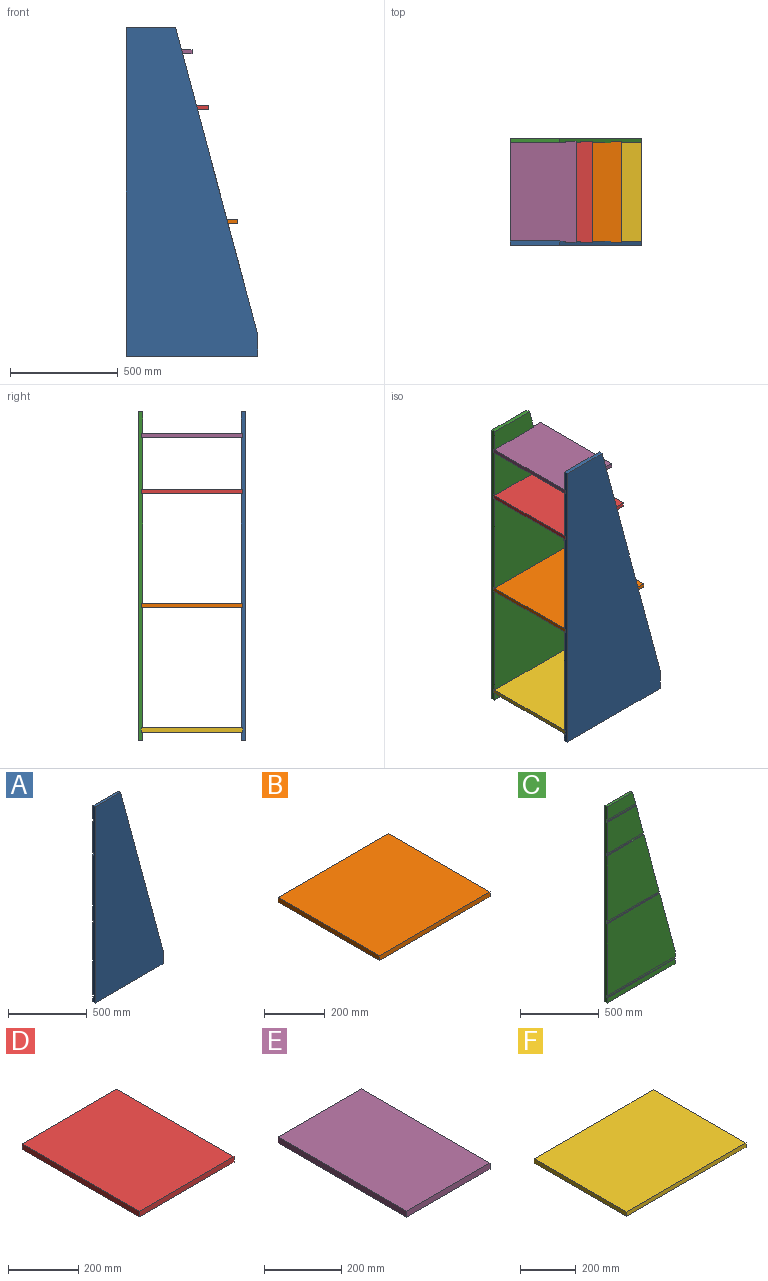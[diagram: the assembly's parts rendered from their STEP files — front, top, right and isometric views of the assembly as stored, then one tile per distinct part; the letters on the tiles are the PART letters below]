
ASSEMBLY  parts=6 mates=16
PART A: 23 faces, bbox 609.6x19.1x1524 mm
  f0: plane 255.81x101.6mm, normal (0,1,0), area 24608.2mm2, adj f5,f6,f7,f17
  f1: plane 508x466.73mm, normal (0,1,0), area 202534.2mm2, adj f5,f7,f11,f15
  f2: plane 609.6x558.8mm, normal (0,1,0), area 305212.9mm2, adj f4,f5,f7,f14,f20
  f3: plane 325.55x241.3mm, normal (0,1,0), area 70757.3mm2, adj f5,f7,f12,f18
  f4: plane 101.6x19.05mm, normal (1,0,0), area 1814.5mm2, adj f2,f5,f8,f9,f10,f20,f21,f22
  f5: plane 1422.4x381mm, normal (0.97,0,0.26), area 27676.2mm2, adj f0,f1,f2,f3,f4,f6,f9,f11
  f6: plane 228.6x19.05mm, normal (0,0,1), area 4354.8mm2, adj f0,f5,f7,f9
  f7: plane 1524x19.05mm, normal (-1,0,0), area 28548.3mm2, adj f0,f1,f2,f3,f6,f8,f9,f10
  f8: plane 609.6x19.05mm, normal (0,0,-1), area 11612.9mm2, adj f4,f7,f9,f10
  f9: plane 1524x609.6mm, normal (0,-1,0), area 658063.2mm2, adj f4,f5,f6,f7,f8
  f10: plane 609.6x38.1mm, normal (0,1,0), area 23225.8mm2, adj f4,f7,f8,f21
  f11: plane 330.65x6.35mm, normal (0,0,1), area 2099.7mm2, adj f1,f5,f7,f13
  f12: plane 325.55x6.35mm, normal (0,0,-1), area 2067.2mm2, adj f3,f5,f7,f13
  f13: plane 330.65x19.05mm, normal (0,1,0), area 6250.3mm2, adj f5,f7,f11,f12
  f14: plane 471.83x6.35mm, normal (0,0,1), area 2996.1mm2, adj f2,f5,f7,f16
  f15: plane 466.73x6.35mm, normal (0,0,-1), area 2963.7mm2, adj f1,f5,f7,f16
  f16: plane 471.83x19.05mm, normal (0,1,0), area 8939.7mm2, adj f5,f7,f14,f15
  f17: plane 255.81x6.35mm, normal (0,0,-1), area 1624.4mm2, adj f0,f5,f7,f19
  f18: plane 260.92x6.35mm, normal (0,0,1), area 1656.8mm2, adj f3,f5,f7,f19
  f19: plane 260.92x19.05mm, normal (0,1,0), area 4921.9mm2, adj f5,f7,f17,f18
  f20: plane 609.6x6.35mm, normal (0,0,-1), area 3871mm2, adj f2,f4,f7,f22
  f21: plane 609.6x6.35mm, normal (0,0,1), area 3871mm2, adj f4,f7,f10,f22
  f22: plane 609.6x19.05mm, normal (0,1,0), area 11612.9mm2, adj f4,f7,f20,f21
PART B: 6 faces, bbox 514.4x469.9x19.1 mm
  f0: plane 514.35x19.05mm, normal (0,1,0), area 9798.4mm2, adj f1,f3,f4,f5
  f1: plane 469.9x19.05mm, normal (-1,0,0), area 8951.6mm2, adj f0,f2,f4,f5
  f2: plane 514.35x19.05mm, normal (0,-1,0), area 9798.4mm2, adj f1,f3,f4,f5
  f3: plane 469.9x19.05mm, normal (1,0,0), area 8951.6mm2, adj f0,f2,f4,f5
  f4: plane 514.35x469.9mm, normal (0,0,1), area 241693.1mm2, adj f0,f1,f2,f3
  f5: plane 514.35x469.9mm, normal (0,0,-1), area 241693.1mm2, adj f0,f1,f2,f3
PART C: 23 faces, bbox 609.6x19.1x1524 mm
  f0: plane 255.81x101.6mm, normal (0,-1,0), area 24608.2mm2, adj f5,f6,f7,f17
  f1: plane 325.55x241.3mm, normal (0,-1,0), area 70757.3mm2, adj f5,f7,f15,f18
  f2: plane 508x466.73mm, normal (0,-1,0), area 202534.2mm2, adj f5,f7,f12,f14
  f3: plane 609.6x558.8mm, normal (0,-1,0), area 305212.9mm2, adj f4,f5,f7,f11,f20
  f4: plane 101.6x19.05mm, normal (1,0,0), area 1814.5mm2, adj f3,f5,f8,f9,f10,f20,f21,f22
  f5: plane 1422.4x381mm, normal (0.97,0,0.26), area 27676.2mm2, adj f0,f1,f2,f3,f4,f6,f10,f11
  f6: plane 228.6x19.05mm, normal (0,0,1), area 4354.8mm2, adj f0,f5,f7,f10
  f7: plane 1524x19.05mm, normal (-1,0,0), area 28548.3mm2, adj f0,f1,f2,f3,f6,f8,f9,f10
  f8: plane 609.6x19.05mm, normal (0,0,-1), area 11612.9mm2, adj f4,f7,f9,f10
  f9: plane 609.6x38.1mm, normal (0,-1,0), area 23225.8mm2, adj f4,f7,f8,f21
  f10: plane 1524x609.6mm, normal (0,1,0), area 658063.2mm2, adj f4,f5,f6,f7,f8
  f11: plane 471.83x6.35mm, normal (0,0,1), area 2996.1mm2, adj f3,f5,f7,f13
  f12: plane 466.73x6.35mm, normal (0,0,-1), area 2963.7mm2, adj f2,f5,f7,f13
  f13: plane 471.83x19.05mm, normal (0,-1,0), area 8939.7mm2, adj f5,f7,f11,f12
  f14: plane 330.65x6.35mm, normal (0,0,1), area 2099.7mm2, adj f2,f5,f7,f16
  f15: plane 325.55x6.35mm, normal (0,0,-1), area 2067.2mm2, adj f1,f5,f7,f16
  f16: plane 330.65x19.05mm, normal (0,-1,0), area 6250.3mm2, adj f5,f7,f14,f15
  f17: plane 255.81x6.35mm, normal (0,0,-1), area 1624.4mm2, adj f0,f5,f7,f19
  f18: plane 260.92x6.35mm, normal (0,0,1), area 1656.8mm2, adj f1,f5,f7,f19
  f19: plane 260.92x19.05mm, normal (0,-1,0), area 4921.9mm2, adj f5,f7,f17,f18
  f20: plane 609.6x6.35mm, normal (0,0,-1), area 3871mm2, adj f3,f4,f7,f22
  f21: plane 609.6x6.35mm, normal (0,0,1), area 3871mm2, adj f4,f7,f9,f22
  f22: plane 609.6x19.05mm, normal (0,-1,0), area 11612.9mm2, adj f4,f7,f20,f21
PART D: 6 faces, bbox 381x469.9x19.1 mm
  f0: plane 381x19.05mm, normal (0,1,0), area 7258mm2, adj f1,f3,f4,f5
  f1: plane 469.9x19.05mm, normal (-1,0,0), area 8951.6mm2, adj f0,f2,f4,f5
  f2: plane 381x19.05mm, normal (0,-1,0), area 7258mm2, adj f1,f3,f4,f5
  f3: plane 469.9x19.05mm, normal (1,0,0), area 8951.6mm2, adj f0,f2,f4,f5
  f4: plane 469.9x381mm, normal (0,0,1), area 179031.9mm2, adj f0,f1,f2,f3
  f5: plane 469.9x381mm, normal (0,0,-1), area 179031.9mm2, adj f0,f1,f2,f3
PART E: 6 faces, bbox 304.8x469.9x19.1 mm
  f0: plane 304.8x19.05mm, normal (0,1,0), area 5806.4mm2, adj f1,f3,f4,f5
  f1: plane 469.9x19.05mm, normal (-1,0,0), area 8951.6mm2, adj f0,f2,f4,f5
  f2: plane 304.8x19.05mm, normal (0,-1,0), area 5806.4mm2, adj f1,f3,f4,f5
  f3: plane 469.9x19.05mm, normal (1,0,0), area 8951.6mm2, adj f0,f2,f4,f5
  f4: plane 469.9x304.8mm, normal (0,0,1), area 143225.5mm2, adj f0,f1,f2,f3
  f5: plane 469.9x304.8mm, normal (0,0,-1), area 143225.5mm2, adj f0,f1,f2,f3
PART F: 6 faces, bbox 609.6x469.9x19.1 mm
  f0: plane 609.6x19.05mm, normal (0,1,0), area 11612.9mm2, adj f1,f3,f4,f5
  f1: plane 469.9x19.05mm, normal (-1,0,0), area 8951.6mm2, adj f0,f2,f4,f5
  f2: plane 609.6x19.05mm, normal (0,-1,0), area 11612.9mm2, adj f1,f3,f4,f5
  f3: plane 469.9x19.05mm, normal (1,0,0), area 8951.6mm2, adj f0,f2,f4,f5
  f4: plane 609.6x469.9mm, normal (0,0,1), area 286451mm2, adj f0,f1,f2,f3
  f5: plane 609.6x469.9mm, normal (0,0,-1), area 286451mm2, adj f0,f1,f2,f3
PLACE A t=(492.27,62.01,681.39)mm
PLACE B t=(444.64,290.61,535.34)mm
PLACE C t=(492.27,538.26,681.39)mm fixed
PLACE D t=(377.97,290.61,1062.39)mm
PLACE E t=(339.87,290.61,1322.74)mm
PLACE F t=(492.27,290.61,-42.51)mm
MATE planar D.f2 <-> A.f13  axis (0,-1,0) through (377.97,55.66,1071.91)mm
MATE planar D.f1 <-> C.f7  axis (-1,0,0) through (187.47,290.61,1071.91)mm
MATE planar A.f8 <-> C.f8  axis (0,0,-1) through (492.27,52.48,-80.61)mm
MATE planar C.f7 <-> D.f1  axis (-1,0,0) through (187.47,528.84,680.58)mm
MATE planar B.f1 <-> C.f7  axis (-1,0,0) through (187.47,290.61,544.86)mm
MATE planar B.f4 <-> C.f12  axis (0,0,1) through (444.64,290.61,554.39)mm
MATE planar F.f4 <-> C.f20  axis (0,0,1) through (492.27,290.61,-23.46)mm
MATE planar C.f7 <-> A.f7  axis (-1,0,0) through (187.47,528.84,680.58)mm
MATE planar F.f0 <-> C.f22  axis (0,1,0) through (492.27,525.56,-32.99)mm
MATE planar F.f2 <-> A.f22  axis (0,-1,0) through (492.27,55.66,-32.99)mm
MATE planar E.f1 <-> C.f7  axis (-1,0,0) through (187.47,290.61,1332.26)mm
MATE planar B.f2 <-> A.f16  axis (0,-1,0) through (444.64,55.66,544.86)mm
MATE planar E.f2 <-> A.f19  axis (0,-1,0) through (339.87,55.66,1332.26)mm
MATE planar E.f4 <-> C.f17  axis (0,0,1) through (339.87,290.61,1341.79)mm
MATE planar F.f1 <-> C.f7  axis (-1,0,0) through (187.47,290.61,-32.99)mm
MATE planar D.f4 <-> C.f15  axis (0,0,1) through (377.97,290.61,1081.44)mm
